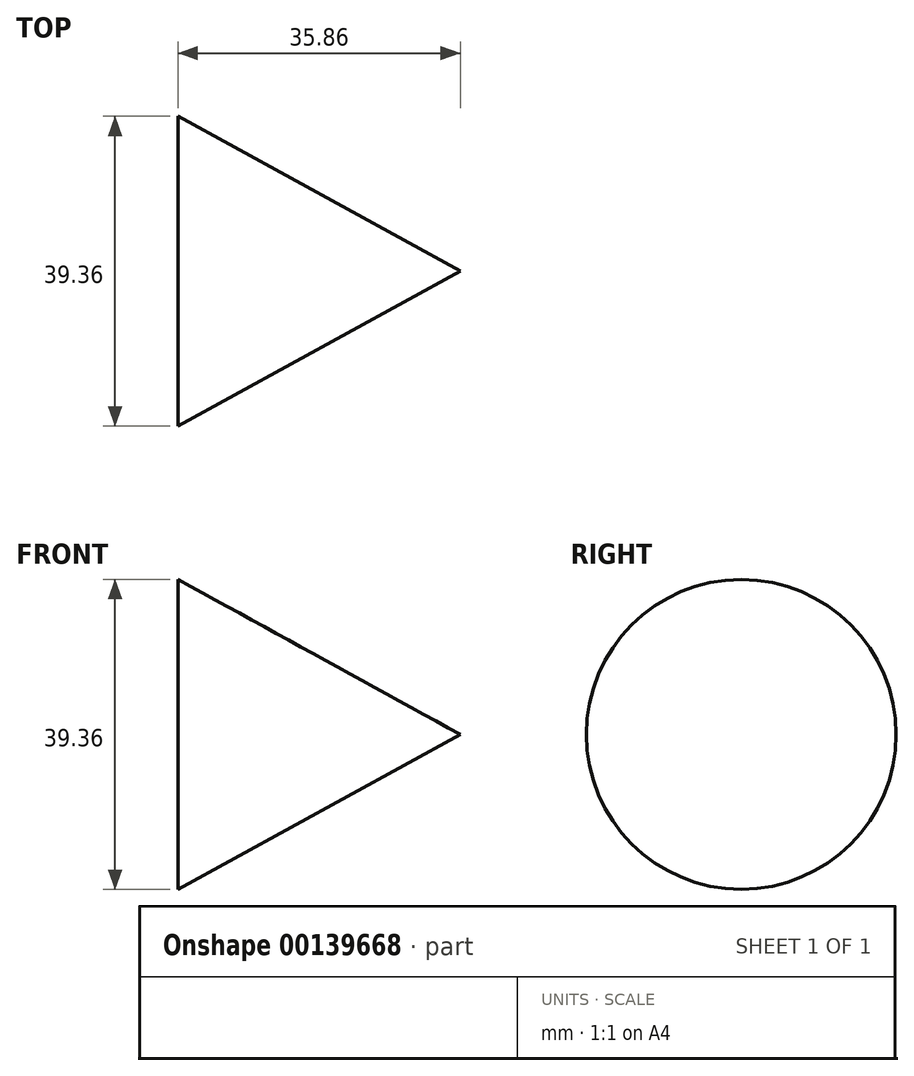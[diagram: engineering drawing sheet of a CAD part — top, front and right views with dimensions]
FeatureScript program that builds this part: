
annotation { "Feature Type Name" : "Feature", "Feature Type Description" : "" }
export const myFeature = defineFeature(function(context is Context, id is Id, definition is map)
    precondition{}
    {
        {
            var Q0;
            Q0=qCreatedBy(makeId("Front.planeOp"),FACE);
            var sketch = newSketch(context, id + "F0", { "sketchPlane" : qUnion([Q0])});
            skLineSegment(sketch, "E0", {"start": v(35.86, 0) * mm, "end": v(0, 19.68) * mm});
            skLineSegment(sketch, "E1", {"start": v(0, 19.68) * mm, "end": v(0, 0) * mm});
            skLineSegment(sketch, "E2", {"start": v(35.86, 0) * mm, "end": v(0, 0) * mm, "construction": true});
            skSolve(sketch);
        }
        {
            var Q0;
            Q0=sQuery(id+"F0.wireOp",EDGE,"E0");
            var Q1;
            Q1=sQuery(id+"F0.wireOp",EDGE,"E1");
            var Q2;
            Q2=sQuery(id+"F0.wireOp",EDGE,"E2");
            revolve(context, id + "F1", {"bodyType" : ToolBodyType.SURFACE, "surfaceEntities" : qUnion([Q0, Q1]), "axis" : qUnion([Q2]), "revolveType" : RevolveType.FULL});
        }
    });
